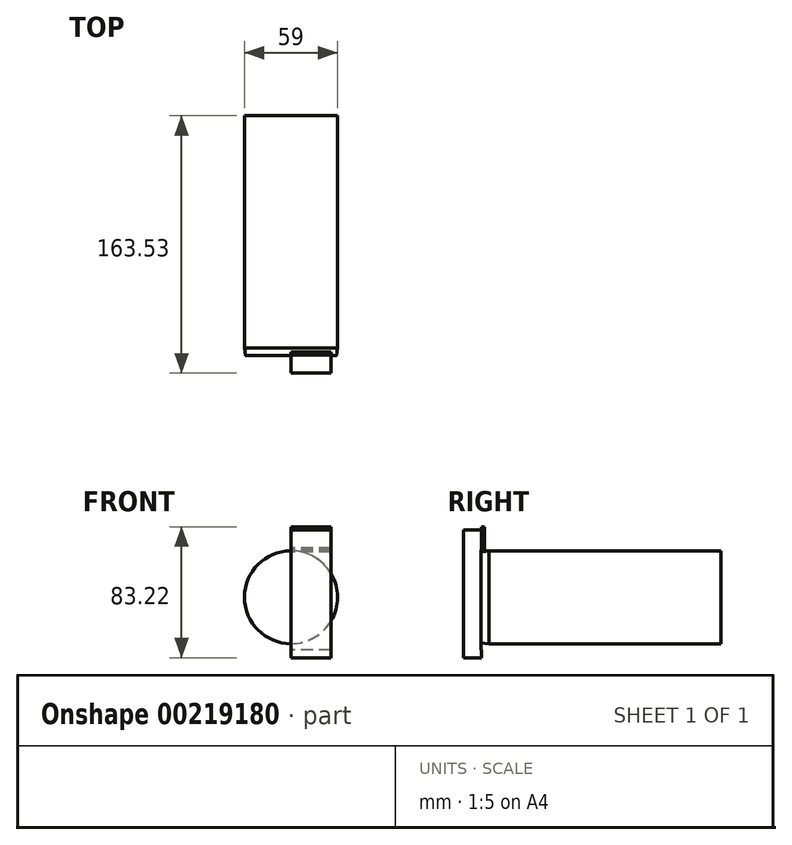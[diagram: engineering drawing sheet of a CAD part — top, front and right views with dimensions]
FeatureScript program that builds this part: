
annotation { "Feature Type Name" : "Feature", "Feature Type Description" : "" }
export const myFeature = defineFeature(function(context is Context, id is Id, definition is map)
    precondition{}
    {
        {
            var Q0;
            Q0=qCreatedBy(makeId("Front.planeOp"),FACE);
            var sketch = newSketch(context, id + "F0", { "sketchPlane" : qUnion([Q0])});
            skCircle(sketch, "E0", {"center": v(0, 0) * mm, "radius": 29.5 * mm});
            skSolve(sketch);
        }
        {
            var Q0;
            Q0 = qSketchRegion(id + "F0", true);
            extrude(context, id + "F1", {"entities" : qUnion([Q0]), "depth" : 152.4 * mm});
        }
        {
            var Q0;
            Q0=qCreatedBy(makeId("Right.planeOp"),FACE);
            var sketch = newSketch(context, id + "F2", { "sketchPlane" : qUnion([Q0])});
            skLineSegment(sketch, "E1", {"start": v(-152.4, 0) * mm, "end": v(12.11, 0) * mm, "construction": true});
            skLineSegment(sketch, "E2.0", {"start": v(-152.4, -29.5) * mm, "end": v(-152.4, 29.5) * mm, "construction": true});
            skLineSegment(sketch, "E3", {"start": v(-152.4, 29.5) * mm, "end": v(-147.4, 29.5) * mm});
            skLineSegment(sketch, "E4", {"start": v(-152.4, 24.5) * mm, "end": v(-152.4, 29.5) * mm});
            skLineSegment(sketch, "E5", {"start": v(-147.4, 29.5) * mm, "end": v(-152.23, 28.88) * mm});
            skArc(sketch, "E6", {"start": v(-152.23, 28.88) * mm, "mid": v(-152.35, 28.8) * mm, "end": v(-152.4, 28.68) * mm});
            skLineSegment(sketch, "E7", {"start": v(-152.4, 28.68) * mm, "end": v(-152.4, 29.5) * mm});
            skSolve(sketch);
        }
        {
            var Q0;
            Q0 = qSketchRegion(id + "F2", true);
            var Q1;
            Q1=sQuery(id+"F2.wireOp",EDGE,"E1");
            revolve(context, id + "F3", {"operationType" : NewBodyOperationType.REMOVE, "entities" : qUnion([Q0]), "axis" : qUnion([Q1]), "revolveType" : RevolveType.FULL, "oppositeDirection" : true});
        }
        {
            var Q0;
            Q0=qCreatedBy(makeId("Right.planeOp"),FACE);
            var sketch = newSketch(context, id + "F4", { "sketchPlane" : qUnion([Q0])});
            skLineSegment(sketch, "E8.bottom", {"start": v(-163.53, 42.85) * mm, "end": v(-152.1, 42.85) * mm});
            skLineSegment(sketch, "E8.top", {"start": v(-163.53, -38.43) * mm, "end": v(-152.1, -38.43) * mm});
            skLineSegment(sketch, "E8.left", {"start": v(-163.53, 42.85) * mm, "end": v(-163.53, -38.43) * mm});
            skLineSegment(sketch, "E8.right", {"start": v(-152.1, 42.85) * mm, "end": v(-152.1, 30.15) * mm});
            skLineSegment(sketch, "E9", {"start": v(-152.4, -33.35) * mm, "end": v(-152.4, 30.15) * mm});
            skLineSegment(sketch, "E10", {"start": v(-152.4, 30.15) * mm, "end": v(-152.1, 30.15) * mm});
            skLineSegment(sketch, "E11", {"start": v(-152.4, -33.35) * mm, "end": v(-152.1, -33.35) * mm});
            skLineSegment(sketch, "E12.trimOffspring", {"start": v(-152.1, -33.35) * mm, "end": v(-152.1, -38.43) * mm});
            skSolve(sketch);
        }
        {
            var Q0;
            Q0 = qSketchRegion(id + "F4", true);
            extrude(context, id + "F5", {"entities" : qUnion([Q0]), "depth" : 25.4 * mm});
        }
        {
            var Q0;
            Q0=qCreatedBy(makeId("Right.planeOp"),FACE);
            var sketch = newSketch(context, id + "F6", { "sketchPlane" : qUnion([Q0])});
            skArc(sketch, "E13", {"start": v(-152.1, 28.92) * mm, "mid": v(-151.3, 29.15) * mm, "end": v(-150.74, 29.79) * mm});
            skLineSegment(sketch, "E14", {"start": v(-152.1, 28.92) * mm, "end": v(-152.1, 44.8) * mm});
            skLineSegment(sketch, "E15", {"start": v(-152.1, 44.8) * mm, "end": v(-150.1, 44.8) * mm});
            skLineSegment(sketch, "E16", {"start": v(-150.74, 29.79) * mm, "end": v(-150.1, 31.16) * mm});
            skLineSegment(sketch, "E17", {"start": v(-150.1, 31.16) * mm, "end": v(-150.1, 44.8) * mm});
            skSolve(sketch);
        }
        {
            var Q0;
            Q0 = qSketchRegion(id + "F6", true);
            extrude(context, id + "F7", {"entities" : qUnion([Q0]), "depth" : 25.4 * mm});
        }
    });
